# Revit family: РИДАН_Компенсатор под приварку с кожухом
name_source: partatom
category: Арматура трубопроводов
units: mm (PartAtom-declared; Revit-internal decimal feet)

## family parameters
Всегда вертикально = Да
На основе рабочей плоскости = Нет
Общий = Нет
При загрузке вырезать с полостями = Нет
Размер круглого соединителя = Использовать диаметр
Тип детали = Вставляется

## types (28) — shared parameters
ADSK_Версия Revit = 2019
ADSK_Версия семейства = 1.0
ADSK_Единица измерения = шт.
ADSK_Завод-изготовитель = ООО «Ридан-Трейд»
ADSK_Количество = 1
ADSK_Марка = Компенсатор
ADSK_Расход жидкости = 0 м³/ч
LT = Table
URL = https://ridan.ru
num = 2
Изготовитель = ООО «Ридан-Трейд»

## per-type parameters (varying)
| type | ADSK_Диаметр условный | ADSK_Код изделия | ADSK_Масса | ADSK_Наименование | a | a1 | b | b2 | c | d | e | num1 |
| DN15  +15/-35mm | 15 мм | 065H0019R | 0.79 | Компенсатор PN16 DN15, перемещение: +15/-35mm, внутренняя гильза/внешний кожух | 280 мм | 280 мм | 20 мм | 20 мм | 45 мм | 155 мм | 180 мм | 1 |
| DN15  +19/-45mm | 15 мм | 065H0001R | 1.04 | Компенсатор PN16 DN15, перемещение: +19/-45mm, внутренняя гильза/внешний кожух | 365 мм | 365 мм | 20 мм | 20 мм | 45 мм | 225 мм | 250 мм | 2 |
| DN20  +15/-35mm | 20 мм | 065H0021R | 0.82 | Компенсатор PN16 DN20, перемещение: +15/-35mm, внутренняя гильза/внешний кожух | 280 мм | 280 мм | 26 мм | 26 мм | 45 мм | 155 мм | 174 мм | 3 |
| DN20  +24/-56mm | 20 мм | 065H0003R | 0.82 | Компенсатор PN16 DN20, перемещение: +24/-56mm, внутренняя гильза/внешний кожух | 450 мм | 450 мм | 26 мм | 26 мм | 45 мм | 295 мм | 314 мм | 4 |
| DN25  +12/-28mm | 25 мм | 065H0022R | 1.07 | Компенсатор PN16 DN25, перемещение: +12/-28mm, внутренняя гильза/внешний кожух | 275 мм | 275 мм | 32 мм | 32 мм | 52 мм | 150 мм | 170 мм | 5 |
| DN25  +19/-45mm | 25 мм | 065H0022R | 1.07 | Компенсатор PN16 DN25, перемещение: +12/-28mm, внутренняя гильза/внешний кожух | 275 мм | 275 мм | 32 мм | 32 мм | 52 мм | 150 мм | 170 мм | 5 |
| DN32  +12/-28mm | 32 мм | 065H0024R | 1.74 | Компенсатор PN16 DN32, перемещение: +12/-28mm, внутренняя гильза/внешний кожух | 310 мм | 310 мм | 42 мм | 42 мм | 63 мм | 163 мм | 184 мм | 7 |
| DN32  +19/-45mm | 32 мм | 065H0025R | 1.9 | Компенсатор PN16 DN32, перемещение: +19/-45mm, внутренняя гильза/внешний кожух | 400 мм | 400 мм | 42 мм | 42 мм | 63 мм | 237 мм | 258 мм | 8 |
| DN40  +11/-25mm | 40 мм | 065H0026R | 0.91 | Компенсатор PN16 DN40, перемещение: +11/-25mm, внутренняя гильза/внешний кожух | 310 мм | 310 мм | 45 мм | 45 мм | 77 мм | 163 мм | 195 мм | 9 |
| DN40  +19/-45mm | 40 мм | 065H0027R | 2.9 | Компенсатор PN16 DN40, перемещение: +19/-45mm, внутренняя гильза/внешний кожух | 400 мм | 400 мм | 45 мм | 45 мм | 77 мм | 237 мм | 269 мм | 10 |
| DN50  +12/-28mm | 50 мм | 065H0028R | 2.5 | Компенсатор PN16 DN50, перемещение: +12/-28mm, внутренняя гильза/внешний кожух | 310 мм | 310 мм | 57 мм | 57 мм | 77 мм | 163 мм | 183 мм | 11 |
| DN50  +19/-45mm | 50 мм | 065H0029R | 3.1 | Компенсатор PN16 DN50, перемещение: +19/-45mm, внутренняя гильза/внешний кожух | 400 мм | 400 мм | 57 мм | 57 мм | 77 мм | 237 мм | 257 мм | 12 |
| DN65  +12 / -28mm | 50 мм | 065H0029R | 3.1 | Компенсатор PN16 DN50, перемещение: +19/-45mm, внутренняя гильза/внешний кожух | 400 мм | 400 мм | 57 мм | 57 мм | 77 мм | 237 мм | 257 мм | 12 |
| DN65  +24 / -56mm | 50 мм | 065H0029R | 3.1 | Компенсатор PN16 DN50, перемещение: +19/-45mm, внутренняя гильза/внешний кожух | 400 мм | 400 мм | 57 мм | 57 мм | 77 мм | 237 мм | 257 мм | 12 |
| DN80  +12 / -28mm | 50 мм | 065H0029R | 3.1 | Компенсатор PN16 DN50, перемещение: +19/-45mm, внутренняя гильза/внешний кожух | 400 мм | 400 мм | 57 мм | 57 мм | 77 мм | 237 мм | 257 мм | 12 |
| DN80  +19 /-45mm | 50 мм | 065H0029R | 3.1 | Компенсатор PN16 DN50, перемещение: +19/-45mm, внутренняя гильза/внешний кожух | 400 мм | 400 мм | 57 мм | 57 мм | 77 мм | 237 мм | 257 мм | 12 |
| DN100  +15 / -33mm | 100 мм | 065H0016R | 5.13 | Компенсатор PN16 DN100, перемещение: +15/-33mm, внутренняя гильза/внешний кожух | 340 мм | 340 мм | 108 мм | 108 мм | 155 мм | 218 мм | 265 мм | 17 |
| DN100  +24 / -56mm | 100 мм | 065H0034R | 5.89 | Компенсатор PN16 DN100, перемещение: +24/-56mm, внутренняя гильза/внешний кожух | 370 мм | 370 мм | 108 мм | 108 мм | 155 мм | 218 мм | 265 мм | 18 |
| DN125  +15 /-35mm | 125 мм | 082X9247R | 5.81 | Осевой сильфонный компенсатор для СО Ду125/Ру16 +15/-35мм с защ. кожухом и  внутр. направляющей, под приварку | 285 мм | 285 мм | 133 мм | 133 мм | 178 мм | 160 мм | 205 мм | 19 |
| DN125  +24 /-56mm | 125 мм | 082X9252R | 7.73 | Осевой сильфонный компенсатор для СО Ду125/Ру16 +24/-56мм с защ. кожухом и внутр. направляющей, под приварку | 375 мм | 375 мм | 133 мм | 133 мм | 178 мм | 248 мм | 293 мм | 20 |
| DN150  +15 /-35mm | 150 мм | 082X9248R | 9 | Осевой сильфонный компенсатор для СО Ду150/Ру16 +15/-35мм с защ. кожухом и  внутр. направляющей, под приварку | 310 мм | 310 мм | 159 мм | 159 мм | 216 мм | 180 мм | 237 мм | 21 |
| DN150  +24 /-56mm | 150 мм | 082X9253R | 10.95 | Осевой сильфонный компенсатор для СО Ду150/Ру16 +24/-56мм с защ. кожухом и внутр. направляющей, под приварку | 415 мм | 415 мм | 159 мм | 159 мм | 216 мм | 288 мм | 345 мм | 22 |
| DN200  +15 /-35mm | 150 мм | 082X9253R | 10.95 | Осевой сильфонный компенсатор для СО Ду150/Ру16 +24/-56мм с защ. кожухом и внутр. направляющей, под приварку | 415 мм | 415 мм | 159 мм | 159 мм | 216 мм | 288 мм | 345 мм | 22 |
| DN200  +24 /-56mm | 150 мм | 082X9253R | 10.95 | Осевой сильфонный компенсатор для СО Ду150/Ру16 +24/-56мм с защ. кожухом и внутр. направляющей, под приварку | 415 мм | 415 мм | 159 мм | 159 мм | 216 мм | 288 мм | 345 мм | 22 |
| DN250  +15 /-35mm | 250 мм | 082X9250R | 17.45 | Осевой сильфонный компенсатор для СО Ду250/Ру16 +15/-35мм с защ. кожухом и  внутр. направляющей, под приварку | 300 мм | 300 мм | 273 мм | 273 мм | 345 мм | 164 мм | 236 мм | 25 |
| DN250  +24 /-56mm | 250 мм | 082X9255R | 27 | Осевой сильфонный компенсатор для СО Ду250/Ру16 +24/-56мм с защ. кожухом и внутр. направляющей, под приварку | 395 мм | 395 мм | 273 мм | 273 мм | 345 мм | 258 мм | 330 мм | 26 |
| DN300  +15 /-35mm | 250 мм | 082X9255R | 27 | Осевой сильфонный компенсатор для СО Ду250/Ру16 +24/-56мм с защ. кожухом и внутр. направляющей, под приварку | 395 мм | 395 мм | 273 мм | 273 мм | 345 мм | 258 мм | 330 мм | 26 |
| DN300  +24 /-56mm | 250 мм | 082X9255R | 27 | Осевой сильфонный компенсатор для СО Ду250/Ру16 +24/-56мм с защ. кожухом и внутр. направляющей, под приварку | 395 мм | 395 мм | 273 мм | 273 мм | 345 мм | 258 мм | 330 мм | 26 |
